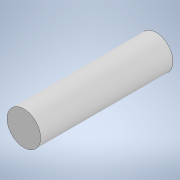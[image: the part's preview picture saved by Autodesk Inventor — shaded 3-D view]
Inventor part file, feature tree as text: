
AUTODESK INVENTOR PART (.ipt)
format: ipt  version: 2022 (Build 260153000, 153)  size: 90,112 bytes
history: native  units: in
note: dims shown in document units (in); Inventor stores cm internally (conversion verified against a paired STEP export)
features: extrude x1, sketch x1
ambient origin geometry x8: Origin, YZ Plane, XZ Plane, XY Plane, X Axis, Y Axis, Z Axis, Center Point
bodies: Solid1 (feature_tree)
feature tree (2):
  extrude  "Extrusion1"  Depth=1.1811in TaperAngle=0.0deg
  sketch  "Sketch1"  dims[d0=0.3in d1=1.1811in d2=0.0in]
